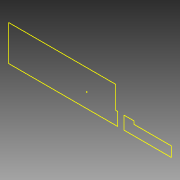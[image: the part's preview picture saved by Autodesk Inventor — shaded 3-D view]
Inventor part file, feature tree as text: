
AUTODESK INVENTOR PART (.ipt)
format: ipt  version: 2014 (Build 180170000, 170)  size: 80,384 bytes
history: native  units: in
note: dims shown in document units (in); Inventor stores cm internally (conversion verified against a paired STEP export)
features: reference x8, extrude x1, sketch x1
ambient origin geometry x8: Origin, YZ Plane, XZ Plane, XY Plane, X Axis, Y Axis, Z Axis, Center Point
bodies: Solid1 (feature_tree)
feature tree (10):
  extrude  "Extrusion1"  [1 undecoded]
  sketch  "Sketch2"  dims[d0=0.0039in d1=0.0in]
  reference  "Reference4"
  reference  "Reference5"
  reference  "Reference6"
  reference  "Reference7"
  reference  "Reference8"
  reference  "Reference9"
  reference  "Reference10"
  reference  "Reference11"
note: 1 required parameter value undecoded (feature->parameter linkage not recoverable at this tier; creation-order binding heuristic only, values carry confidence <= 0.55)
